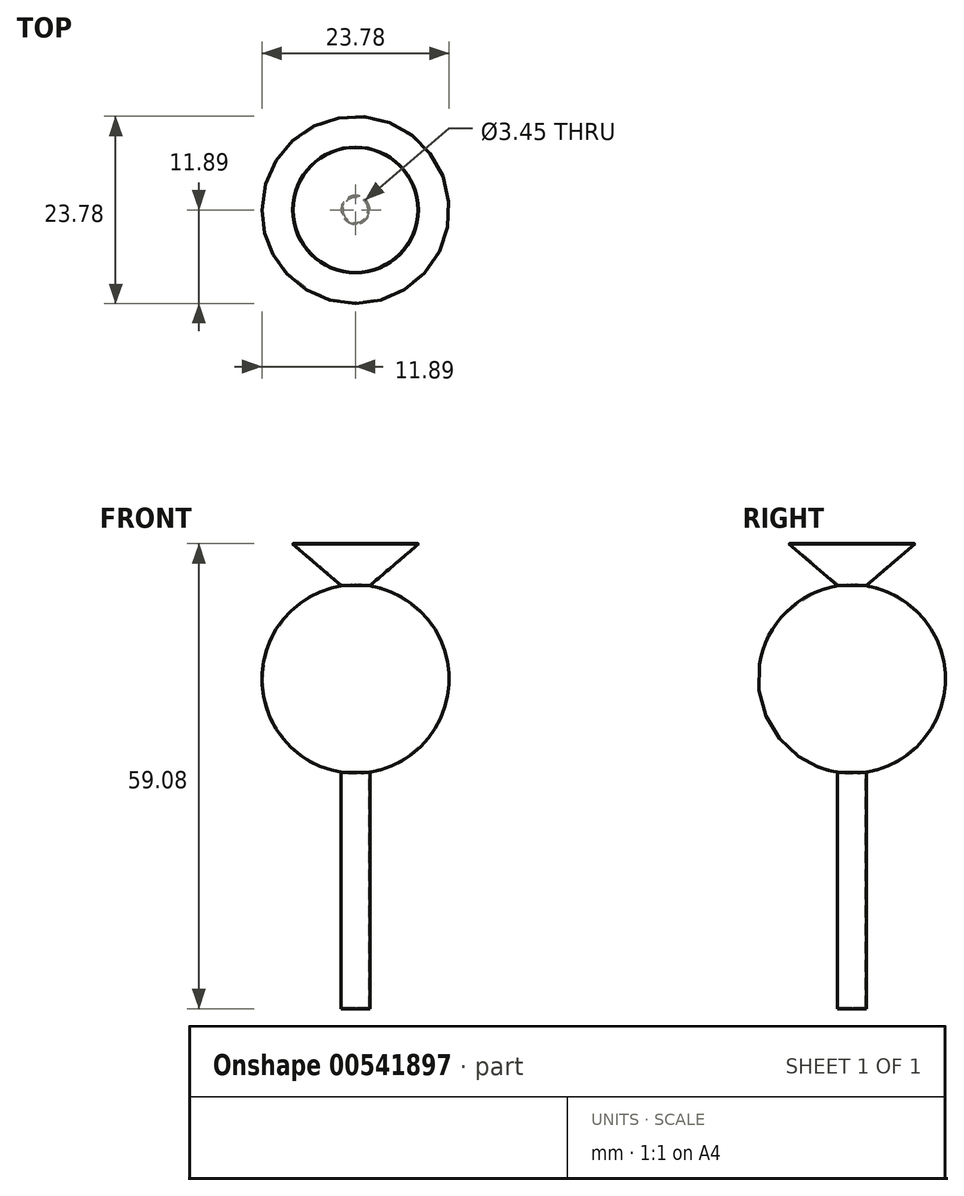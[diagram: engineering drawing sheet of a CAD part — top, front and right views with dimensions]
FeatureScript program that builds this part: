
annotation { "Feature Type Name" : "Feature", "Feature Type Description" : "" }
export const myFeature = defineFeature(function(context is Context, id is Id, definition is map)
    precondition{}
    {
        {
            var Q0;
            Q0=qCreatedBy(makeId("Front.planeOp"),FACE);
            var sketch = newSketch(context, id + "F0", { "sketchPlane" : qUnion([Q0])});
            skArc(sketch, "E0", {"start": v(7.99, 29) * mm, "mid": v(4, 31.12) * mm, "end": v(0, 29) * mm});
            skLineSegment(sketch, "E1", {"start": v(7.99, 29) * mm, "end": v(1.83, 23.75) * mm});
            skArc(sketch, "E2", {"start": v(1.83, 0) * mm, "mid": v(12.1, 11.88) * mm, "end": v(1.83, 23.75) * mm});
            skLineSegment(sketch, "E3", {"start": v(1.83, -30) * mm, "end": v(1.83, 0) * mm});
            skLineSegment(sketch, "E4", {"start": v(1.83, -30) * mm, "end": v(0, -30) * mm});
            skPoint(sketch, "E5.end.orphan", {"position": v(0, 0) * mm});
            skLineSegment(sketch, "E6", {"start": v(0, 29) * mm, "end": v(0, -30) * mm});
            skSolve(sketch);
        }
        {
            var Q0;
            Q0=makeQuery(id+"F0.imprint","IMPRINT",FACE,{"disambiguationData":[TD([[makeQuery(id+"F0.imprint","IMPRINT",EDGE,{"derivedFrom":sQuery(id+"F0.wireOp",EDGE,"E0")}),1.0]])]});
            var Q1;
            Q1=sQuery(id+"F0.wireOp",EDGE,"E6");
            revolve(context, id + "F1", {"entities" : qUnion([Q0]), "axis" : qUnion([Q1]), "revolveType" : RevolveType.FULL});
        }
        {
            var Q0;
            Q0=makeQuery(id+"F1.opRevolve","SWEPT_FACE",FACE,{"disambiguationData":[OSD([sQuery(id+"F0.wireOp",EDGE,"E0")])]});
            shell(context, id + "F2", {"entities" : qUnion([Q0]), "thickness" : 0.1 * mm});
        }
    });
